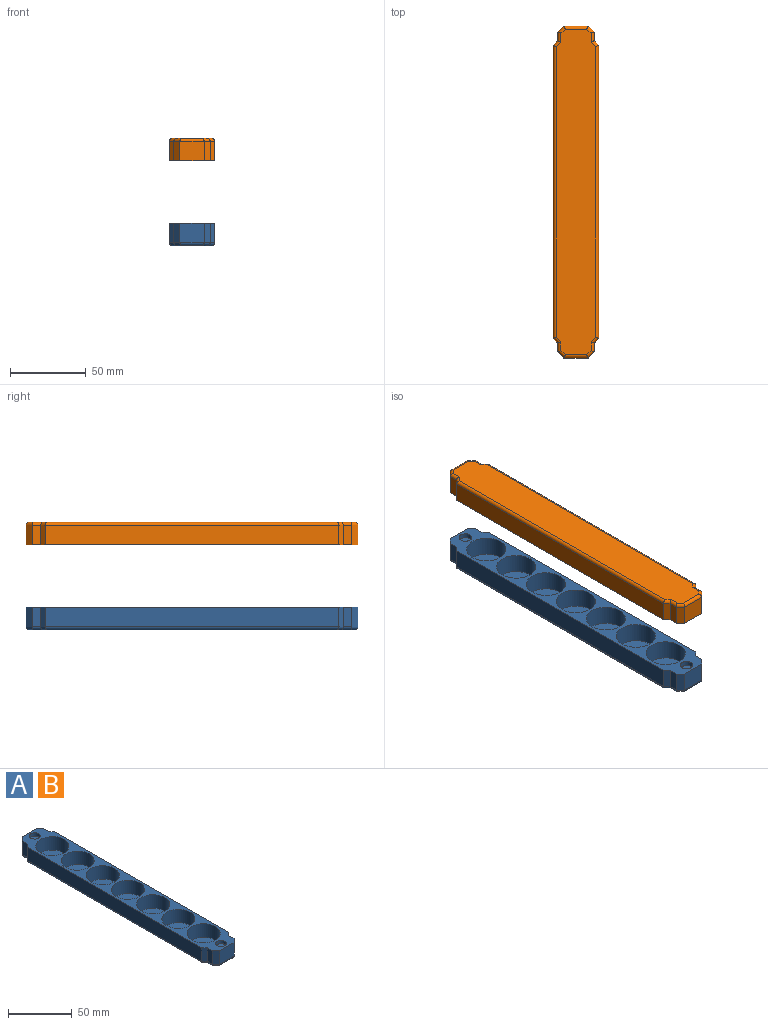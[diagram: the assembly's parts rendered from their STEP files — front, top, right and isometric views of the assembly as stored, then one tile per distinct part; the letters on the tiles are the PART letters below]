
ASSEMBLY  parts=2 mates=1
PART A: 52 faces, bbox 30x219.6x15 mm
  f0: plane 219.64x30mm, normal (0,0,1), area 2591.3mm2, adj f1,f2,f4,f6,f8,f10,f12,f14
  f1: plane 194x13mm, normal (1,0,0), area 2522mm2, adj f0,f19,f20,f42
  f2: plane 194x13mm, normal (-1,0,0), area 2522mm2, adj f0,f18,f21,f45
  f3: plane 215.64x26mm, normal (0,0,-1), area 5468.8mm2, adj f36,f37,f38,f39,f40,f41,f42,f43
  f4: cylinder r=13mm len=26mm, axis (0,0,1), area 1061.9mm2, adj f0,f5
  f5: plane 26x26mm, normal (0,0,1), area 530.9mm2, adj f4
  f6: cylinder r=13mm len=26mm, axis (0,0,1), area 1061.9mm2, adj f0,f7
  f7: plane 26x26mm, normal (0,0,1), area 530.9mm2, adj f6
  f8: cylinder r=13mm len=26mm, axis (0,0,1), area 1061.9mm2, adj f0,f9
  f9: plane 26x26mm, normal (0,0,1), area 530.9mm2, adj f8
  f10: cylinder r=13mm len=26mm, axis (0,0,1), area 1061.9mm2, adj f0,f11
  f11: plane 26x26mm, normal (0,0,1), area 530.9mm2, adj f10
  f12: cylinder r=13mm len=26mm, axis (0,0,1), area 1061.9mm2, adj f0,f13
  f13: plane 26x26mm, normal (0,0,1), area 530.9mm2, adj f12
  f14: cylinder r=13mm len=26mm, axis (0,0,1), area 1061.9mm2, adj f0,f15
  f15: plane 26x26mm, normal (0,0,1), area 530.9mm2, adj f14
  f16: cylinder r=13mm len=26mm, axis (0,0,1), area 1061.9mm2, adj f0,f17
  f17: plane 26x26mm, normal (0,0,1), area 530.9mm2, adj f16
  f18: plane 13x3mm, normal (-0.71,0.71,0), area 55.2mm2, adj f0,f2,f22,f47
  f19: plane 13x3mm, normal (0.71,0.71,0), area 55.2mm2, adj f0,f1,f23,f44
  f20: plane 13x3mm, normal (0.71,-0.71,0), area 55.2mm2, adj f0,f1,f27,f40
  f21: plane 13x3mm, normal (-0.71,-0.71,0), area 55.2mm2, adj f0,f2,f25,f43
  f22: plane 13x5.82mm, normal (-1,0,0), area 75.6mm2, adj f0,f18,f28,f49
  f23: plane 13x5.82mm, normal (1,0,0), area 75.6mm2, adj f0,f19,f29,f46
  f24: plane 16x13mm, normal (0,1,0), area 208mm2, adj f0,f28,f29,f50
  f25: plane 13x5.82mm, normal (-1,0,0), area 75.6mm2, adj f0,f21,f31,f41
  f26: plane 16x13mm, normal (0,-1,0), area 208mm2, adj f0,f30,f31,f37
  f27: plane 13x5.82mm, normal (1,0,0), area 75.6mm2, adj f0,f20,f30,f38
  f28: plane 13x4mm, normal (-0.71,0.71,0), area 73.5mm2, adj f0,f22,f24,f51
  f29: plane 13x4mm, normal (0.71,0.71,0), area 73.5mm2, adj f0,f23,f24,f48
  f30: plane 13x4mm, normal (0.71,-0.71,0), area 73.5mm2, adj f0,f26,f27,f36
  f31: plane 13x4mm, normal (-0.71,-0.71,0), area 73.5mm2, adj f0,f25,f26,f39
  f32: cylinder r=4.25mm len=8.5mm, axis (0,0,1), area 85.5mm2, adj f0,f33
  f33: plane 8.5x8.5mm, normal (0,0,1), area 56.7mm2, adj f32
  f34: cylinder r=4.25mm len=8.5mm, axis (0,0,1), area 85.5mm2, adj f0,f35
  f35: plane 8.5x8.5mm, normal (0,0,1), area 56.7mm2, adj f34
  f36: cylinder r=2mm len=5.41mm, axis (0.71,0.71,0), area 15.9mm2, adj f3,f30,f37,f38
  f37: cylinder r=2mm len=16mm, axis (-1,0,0), area 48.4mm2, adj f3,f26,f36,f39
  f38: cylinder r=2mm len=6.65mm, axis (0,-1,0), area 18.3mm2, adj f3,f27,f36,f40
  f39: cylinder r=2mm len=5.41mm, axis (-0.71,0.71,0), area 15.9mm2, adj f3,f31,f37,f41
  f40: cylinder r=2mm len=5mm, axis (-0.71,-0.71,0), area 13.3mm2, adj f3,f20,f38,f42
  f41: cylinder r=2mm len=6.65mm, axis (0,1,0), area 18.3mm2, adj f3,f25,f39,f43
  f42: cylinder r=2mm len=194mm, axis (0,1,0), area 607.6mm2, adj f1,f3,f40,f44
  f43: cylinder r=2mm len=5mm, axis (0.71,-0.71,0), area 13.3mm2, adj f3,f21,f41,f45
  f44: cylinder r=2mm len=5mm, axis (-0.71,0.71,0), area 13.3mm2, adj f3,f19,f42,f46
  f45: cylinder r=2mm len=194mm, axis (0,-1,0), area 607.6mm2, adj f2,f3,f43,f47
  f46: cylinder r=2mm len=6.65mm, axis (0,-1,0), area 18.3mm2, adj f3,f23,f44,f48
  f47: cylinder r=2mm len=5mm, axis (0.71,0.71,0), area 13.3mm2, adj f3,f18,f45,f49
  f48: cylinder r=2mm len=5.41mm, axis (-0.71,0.71,0), area 15.9mm2, adj f3,f29,f46,f50
  f49: cylinder r=2mm len=6.65mm, axis (0,1,0), area 18.3mm2, adj f3,f22,f47,f51
  f50: cylinder r=2mm len=16mm, axis (1,0,0), area 48.4mm2, adj f3,f24,f48,f51
  f51: cylinder r=2mm len=5.41mm, axis (0.71,0.71,0), area 15.9mm2, adj f3,f28,f49,f50
PART B: same geometry as A
PLACE A t=(3.15,2.97,-81.52)mm
PLACE B rot(axis=(0,1,0),180deg) t=(3.15,2.97,-10.39)mm
MATE planar B.f2 <-> A.f1  axis (1,0,0) through (18.15,2.97,-18.89)mm
